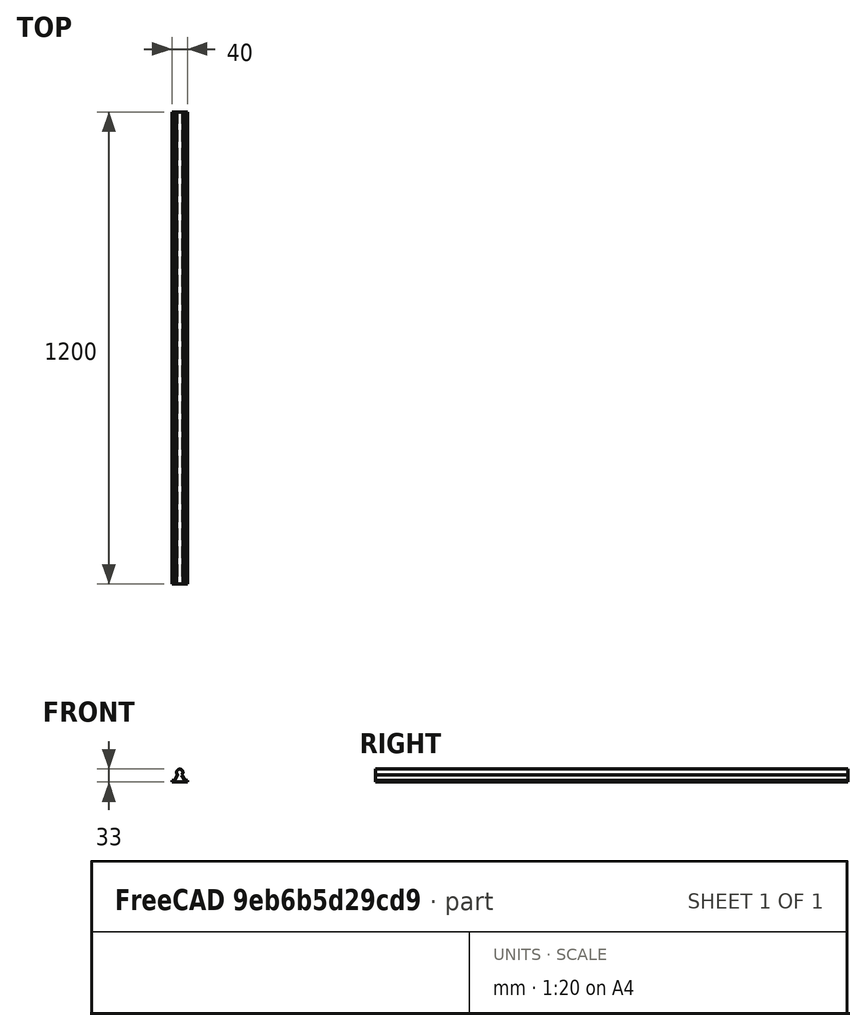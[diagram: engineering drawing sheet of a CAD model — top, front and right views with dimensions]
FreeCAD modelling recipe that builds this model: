
FCSTD DOCUMENT  (FreeCAD 1.0R39319 (Git))
Label: SBR16 rail
License: All rights reserved
LicenseURL: https://en.wikipedia.org/wiki/All_rights_reserved
objects: Sketcher::SketchObject×1, PartDesign::Pad×1, PartDesign::Body×1
note: 6 computed .brp shape members not serialized (recipe doc carries the construction recipe); baked Part::Feature solids carry a one-line shape summary decoded from their .brp

FEATURE [Sketcher::SketchObject] Sketch
  ArcFitTolerance = 1e-06
  AttachmentSupport = -> [XZ_Plane]
  FullyConstrained = true
  MakeInternals = false
  MapMode = 5
  Placement = pos=(0,0,0) rot=(1,0,0;1.5708rad)
  sketch-geometry (8):
    g0: ArcOfCircle CenterX=0 CenterY=0 CenterZ=0 NormalX=0 NormalY=0 NormalZ=1 AngleXU=0 Radius=8 StartAngle=5.38752 EndAngle=10.3204
    g1: LineSegment StartX=-20 StartY=-25 StartZ=0 EndX=20 EndY=-25 EndZ=0
    g2: LineSegment StartX=-20 StartY=-25 StartZ=0 EndX=-20 EndY=-20 EndZ=0
    g3: LineSegment StartX=20 StartY=-25 StartZ=0 EndX=20 EndY=-20 EndZ=0
    g4: LineSegment StartX=5 StartY=-6.245 StartZ=0 EndX=12.9414 EndY=-20 EndZ=0
    g5: LineSegment StartX=-5 StartY=-6.245 StartZ=0 EndX=-12.9415 EndY=-20 EndZ=0
    g6: LineSegment StartX=-20 StartY=-20 StartZ=0 EndX=-12.9415 EndY=-20 EndZ=0
    g7: LineSegment StartX=12.9414 StartY=-20 StartZ=0 EndX=20 EndY=-20 EndZ=0
  constraints (25):
    c: Diameter(g0) = 16
    c: Coincident(g0,g-1)
    c: Distance(g1) = 40
    c: Horizontal(g1)
    c: DistanceX(g1) = -20
    c: DistanceY(g1) = -25
    c: Distance(g2) = 5
    c: Coincident(g2,g1)
    c: Vertical(g2)
    c: Distance(g3) = 5
    c: Coincident(g3,g1)
    c: Vertical(g3)
    c: Angle(g-1,g4) = -1.0472
    c: Angle(g-1,g5) = -2.0944
    c: Coincident(g6,g2)
    c: Coincident(g7,g3)
    c: PointOnObject(g4,g7)
    c: Coincident(g0,g5)
    c: Coincident(g0,g4)
    c: Coincident(g6,g5)
    c: PointOnObject(g7,g4)
    c: DistanceX(g0,g0) = 10
    c: Horizontal(g6)
    c: Horizontal(g7)
    c: Distance(g0,g-2) = 5
FEATURE [PartDesign::Pad] Pad
  Direction = (0,-1,2e-16)
  Length = 1200
  Length2 = 10
  Placement = pos=(0,0,0) rot=(1,0,0;1.5708rad)
  Profile = -> Sketch
  ReferenceAxis = -> Sketch [N_Axis]
  Refine = true
  Suppressed = false
  Type = 0
FEATURE [PartDesign::Body] Body
  AllowCompound = false
  Group = -> [Sketch,Pad]
  Origin = -> Origin
  Tip = -> Pad
